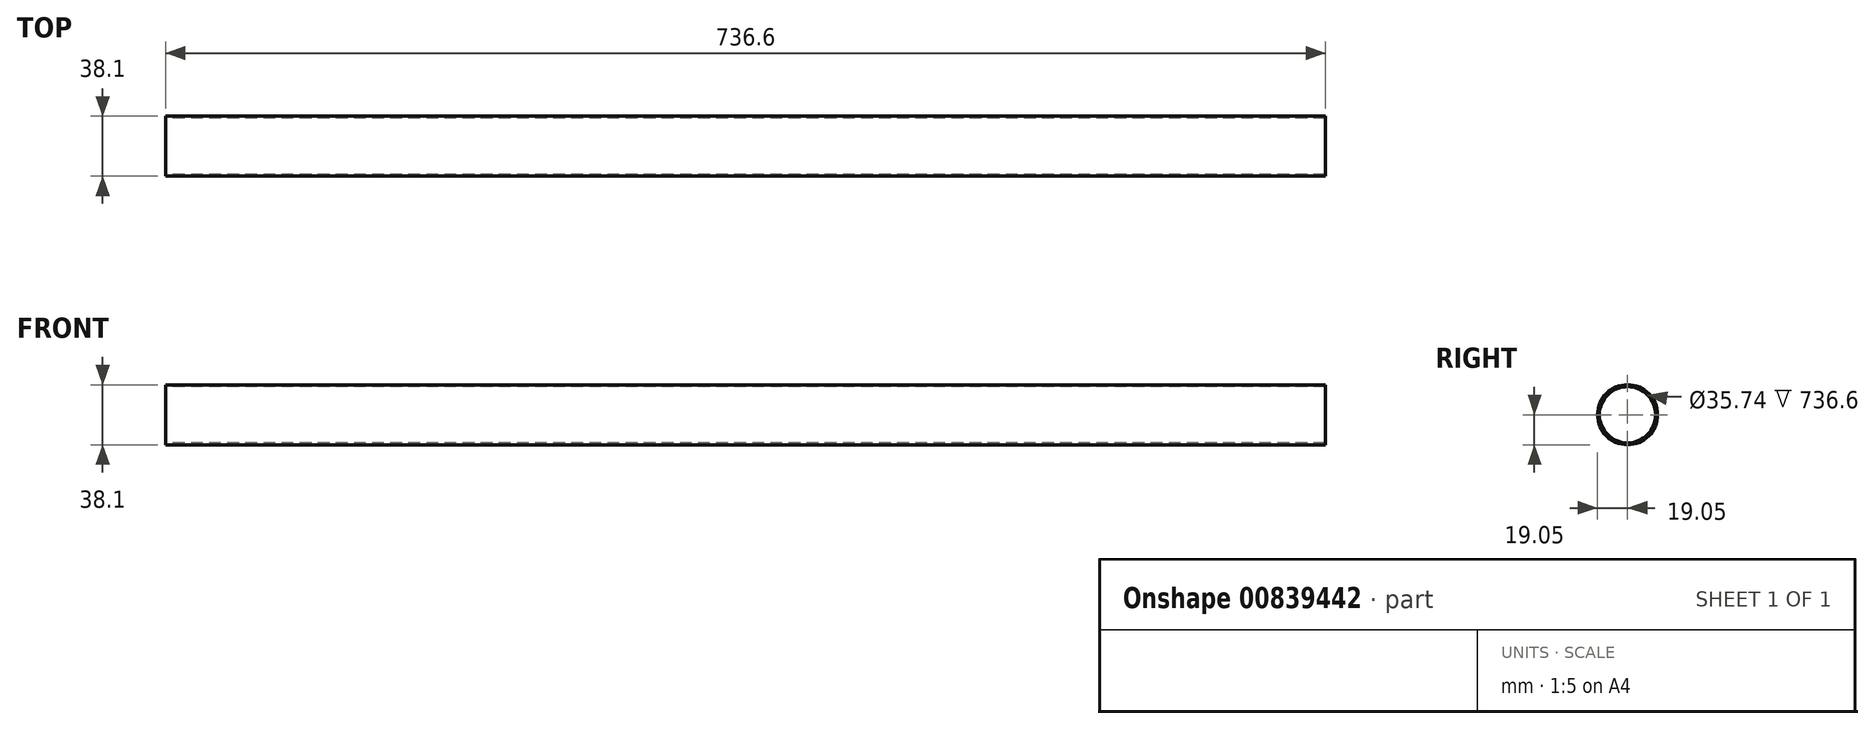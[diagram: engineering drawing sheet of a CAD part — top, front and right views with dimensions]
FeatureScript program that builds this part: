
annotation { "Feature Type Name" : "Feature", "Feature Type Description" : "" }
export const myFeature = defineFeature(function(context is Context, id is Id, definition is map)
    precondition{}
    {
        {
            var Q0;
            Q0=qCreatedBy(makeId("Right.planeOp"),FACE);
            var sketch = newSketch(context, id + "F0", { "sketchPlane" : qUnion([Q0])});
            skCircle(sketch, "E0", {"center": v(0, 0) * mm, "radius": 19.05 * mm});
            skCircle(sketch, "E1", {"center": v(0, 0) * mm, "radius": 17.87 * mm});
            skSolve(sketch);
        }
        {
            var Q0;
            Q0=makeQuery(id+"F0.imprint","IMPRINT",FACE,{"disambiguationData":[TD([[makeQuery(id+"F0.imprint","IMPRINT",EDGE,{"derivedFrom":sQuery(id+"F0.wireOp",EDGE,"E0")}),1.0]])]});
            extrude(context, id + "F1", {"entities" : qUnion([Q0]), "depth" : 736.6 * mm, "offsetDistance" : 25.4 * mm, "symmetric" : true});
        }
    });
